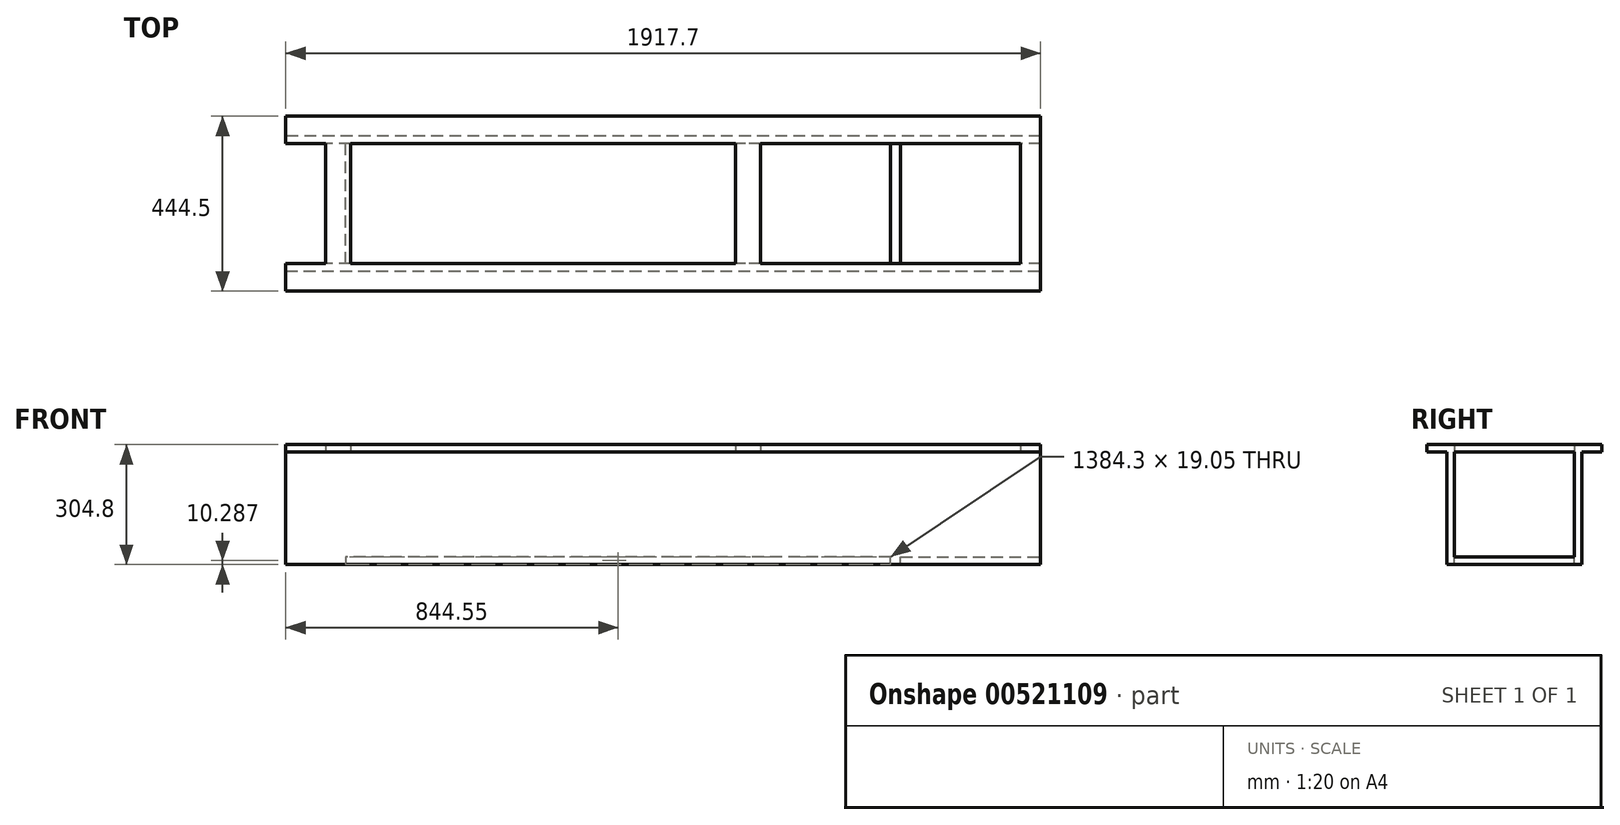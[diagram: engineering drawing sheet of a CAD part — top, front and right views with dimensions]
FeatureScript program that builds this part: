
annotation { "Feature Type Name" : "Feature", "Feature Type Description" : "" }
export const myFeature = defineFeature(function(context is Context, id is Id, definition is map)
    precondition{}
    {
        {
            var Q0;
            Q0=qCreatedBy(makeId("Front.planeOp"),FACE);
            var sketch = newSketch(context, id + "F0", { "sketchPlane" : qUnion([Q0])});
            skLineSegment(sketch, "E0.bottom", {"start": v(831.85, 152.4) * mm, "end": v(-831.85, 152.4) * mm});
            skLineSegment(sketch, "E0.top", {"start": v(831.85, -152.4) * mm, "end": v(-831.85, -152.4) * mm});
            skLineSegment(sketch, "E0.left", {"start": v(831.85, 152.4) * mm, "end": v(831.85, -152.4) * mm});
            skLineSegment(sketch, "E0.right", {"start": v(-831.85, 152.4) * mm, "end": v(-831.85, -152.4) * mm});
            skPoint(sketch, "E0.middle", {"position": v(0, 0) * mm});
            skSolve(sketch);
        }
        {
            var Q0;
            Q0=makeQuery(id+"F0.imprint","IMPRINT",FACE,{"disambiguationData":[TD([[makeQuery(id+"F0.imprint","IMPRINT",EDGE,{"derivedFrom":sQuery(id+"F0.wireOp",EDGE,"E0.bottom")}),1.0]])]});
            extrude(context, id + "F1", {"entities" : qUnion([Q0]), "depth" : 19.05 * mm, "offsetDistance" : 25.4 * mm});
        }
        {
            var Q0;
            Q0=makeQuery(id+"F1.opExtrude","CAP_FACE",FACE,{"disambiguationData":[OSD([sQuery(id+"F0.wireOp",EDGE,"E0.bottom"),sQuery(id+"F0.wireOp",EDGE,"E0.top"),sQuery(id+"F0.wireOp",EDGE,"E0.left"),sQuery(id+"F0.wireOp",EDGE,"E0.right")])],"isStart":false});
            var sketch = newSketch(context, id + "F2", { "sketchPlane" : qUnion([Q0])});
            skLineSegment(sketch, "E1", {"start": v(831.85, -152.4) * mm, "end": v(831.85, -151.64) * mm});
            skLineSegment(sketch, "E2", {"start": v(831.85, -151.64) * mm, "end": v(781.05, -151.64) * mm});
            skLineSegment(sketch, "E3", {"start": v(781.05, -151.64) * mm, "end": v(781.05, -132.59) * mm});
            skLineSegment(sketch, "E4", {"start": v(781.05, -132.59) * mm, "end": v(831.85, -132.59) * mm});
            skLineSegment(sketch, "E5", {"start": v(831.85, -132.59) * mm, "end": v(831.85, -151.64) * mm});
            skSolve(sketch);
        }
        {
            var Q0;
            Q0 = qSketchRegion(id + "F2", true);
            extrude(context, id + "F3", {"entities" : qUnion([Q0]), "operationType" : NewBodyOperationType.ADD, "depth" : 304.8 * mm, "offsetDistance" : 25.4 * mm});
        }
        {
            var Q0;
            Q0=makeQuery(id+"F1.opExtrude","CAP_FACE",FACE,{"disambiguationData":[OSD([sQuery(id+"F0.wireOp",EDGE,"E0.bottom"),sQuery(id+"F0.wireOp",EDGE,"E0.top"),sQuery(id+"F0.wireOp",EDGE,"E0.left"),sQuery(id+"F0.wireOp",EDGE,"E0.right")])],"isStart":false});
            var sketch = newSketch(context, id + "F4", { "sketchPlane" : qUnion([Q0])});
            skLineSegment(sketch, "E6", {"start": v(781.05, -151.64) * mm, "end": v(476.25, -151.64) * mm});
            skLineSegment(sketch, "E7", {"start": v(476.25, -151.64) * mm, "end": v(476.25, -132.59) * mm});
            skLineSegment(sketch, "E8", {"start": v(476.25, -132.59) * mm, "end": v(-831.85, -132.59) * mm});
            skLineSegment(sketch, "E9", {"start": v(476.25, -151.64) * mm, "end": v(-831.85, -151.64) * mm});
            skLineSegment(sketch, "E10", {"start": v(-831.85, -151.64) * mm, "end": v(-831.85, -132.59) * mm});
            skSolve(sketch);
        }
        {
            var Q0;
            Q0=makeQuery(id+"F4.imprint","IMPRINT",FACE,{"disambiguationData":[TD([[makeQuery(id+"F4.imprint","IMPRINT",EDGE,{"derivedFrom":sQuery(id+"F4.wireOp",EDGE,"E7")}),1.0]])]});
            extrude(context, id + "F5", {"entities" : qUnion([Q0]), "operationType" : NewBodyOperationType.ADD, "depth" : 304.8 * mm, "offsetDistance" : 25.4 * mm});
        }
        {
            var Q0;
            Q0=makeQuery(id+"F5.opExtrude","CAP_FACE",FACE,{"disambiguationData":[OSD([sQuery(id+"F4.wireOp",EDGE,"E7"),sQuery(id+"F4.wireOp",EDGE,"E8"),sQuery(id+"F4.wireOp",EDGE,"E9"),sQuery(id+"F4.wireOp",EDGE,"E10")])],"isStart":false});
            var sketch = newSketch(context, id + "F6", { "sketchPlane" : qUnion([Q0])});
            skLineSegment(sketch, "E11", {"start": v(-831.85, -151.64) * mm, "end": v(-831.85, -152.4) * mm});
            skLineSegment(sketch, "E12", {"start": v(-831.85, -152.4) * mm, "end": v(831.85, -152.4) * mm});
            skLineSegment(sketch, "E13", {"start": v(831.85, -152.4) * mm, "end": v(831.85, 152.4) * mm});
            skLineSegment(sketch, "E14", {"start": v(831.85, 152.4) * mm, "end": v(-831.85, 152.4) * mm});
            skLineSegment(sketch, "E15", {"start": v(-831.85, 152.4) * mm, "end": v(-831.85, -152.4) * mm});
            skSolve(sketch);
        }
        {
            var Q0;
            Q0 = qSketchRegion(id + "F6", true);
            extrude(context, id + "F7", {"entities" : qUnion([Q0]), "operationType" : NewBodyOperationType.ADD, "depth" : 19.05 * mm, "offsetDistance" : 25.4 * mm});
        }
        {
            var Q0;
            Q0=makeQuery(id+"F7.opExtrude","SWEPT_FACE",FACE,{"disambiguationData":[OSD([sQuery(id+"F6.wireOp",EDGE,"E14")])]});
            extrude(context, id + "F8", {"entities" : qUnion([Q0]), "operationType" : NewBodyOperationType.REMOVE, "oppositeDirection" : true, "depth" : 19.05 * mm, "offsetDistance" : 25.4 * mm});
        }
        {
            var Q0;
            Q0=makeQuery(id+"F1.opExtrude","SWEPT_FACE",FACE,{"disambiguationData":[OSD([sQuery(id+"F0.wireOp",EDGE,"E0.bottom")])]});
            extrude(context, id + "F9", {"entities" : qUnion([Q0]), "operationType" : NewBodyOperationType.REMOVE, "oppositeDirection" : true, "depth" : 19.05 * mm, "offsetDistance" : 25.4 * mm});
        }
        {
            var Q0;
            Q0=makeQuery(id+"F8.boolean.opBoolean","COPY",FACE,{"derivedFrom":makeQuery(id+"F8.opExtrude","CAP_FACE",FACE,{"disambiguationData":[OSD([sQuery(id+"F6.wireOp",EDGE,"E14")])],"isStart":false})});
            var sketch = newSketch(context, id + "F10", { "sketchPlane" : qUnion([Q0])});
            skLineSegment(sketch, "E16", {"start": v(831.85, -342.9) * mm, "end": v(831.85, -393.7) * mm});
            skLineSegment(sketch, "E17", {"start": v(831.85, -393.7) * mm, "end": v(-831.85, -393.7) * mm});
            skLineSegment(sketch, "E18", {"start": v(-831.85, -393.7) * mm, "end": v(-831.85, -323.85) * mm});
            skLineSegment(sketch, "E19", {"start": v(-831.85, -323.85) * mm, "end": v(-679.45, -323.85) * mm});
            skLineSegment(sketch, "E20", {"start": v(-679.45, -323.85) * mm, "end": v(-679.45, -19.05) * mm});
            skLineSegment(sketch, "E21", {"start": v(-679.45, -19.05) * mm, "end": v(-831.85, -19.05) * mm});
            skLineSegment(sketch, "E22", {"start": v(-831.85, -19.05) * mm, "end": v(-831.85, 50.8) * mm});
            skLineSegment(sketch, "E23", {"start": v(-831.85, 50.8) * mm, "end": v(831.85, 50.8) * mm});
            skLineSegment(sketch, "E24", {"start": v(831.85, 50.8) * mm, "end": v(831.85, -19.05) * mm});
            skLineSegment(sketch, "E25", {"start": v(831.85, -19.05) * mm, "end": v(831.85, -323.85) * mm});
            skLineSegment(sketch, "E26", {"start": v(831.85, -323.85) * mm, "end": v(831.85, -342.9) * mm});
            skLineSegment(sketch, "E27", {"start": v(831.85, -19.05) * mm, "end": v(781.05, -19.05) * mm});
            skLineSegment(sketch, "E28", {"start": v(781.05, -19.05) * mm, "end": v(781.05, -323.85) * mm});
            skLineSegment(sketch, "E29", {"start": v(781.05, -323.85) * mm, "end": v(425.45, -323.85) * mm});
            skLineSegment(sketch, "E30", {"start": v(425.45, -323.85) * mm, "end": v(425.45, -19.05) * mm});
            skLineSegment(sketch, "E31", {"start": v(425.45, -19.05) * mm, "end": v(781.05, -19.05) * mm});
            skLineSegment(sketch, "E32", {"start": v(425.45, -19.05) * mm, "end": v(361.95, -19.05) * mm});
            skLineSegment(sketch, "E33", {"start": v(361.95, -19.05) * mm, "end": v(361.95, -323.85) * mm});
            skLineSegment(sketch, "E34", {"start": v(361.95, -323.85) * mm, "end": v(-679.45, -323.85) * mm});
            skLineSegment(sketch, "E35", {"start": v(-679.45, -323.85) * mm, "end": v(-615.95, -323.85) * mm});
            skLineSegment(sketch, "E36", {"start": v(-615.95, -323.85) * mm, "end": v(-615.95, -19.05) * mm});
            skLineSegment(sketch, "E37", {"start": v(-615.95, -19.05) * mm, "end": v(361.95, -19.05) * mm});
            skSolve(sketch);
        }
        {
            var Q0;
            Q0 = qSketchRegion(id + "F10", true);
            extrude(context, id + "F11", {"entities" : qUnion([Q0]), "operationType" : NewBodyOperationType.ADD, "depth" : 19.05 * mm, "offsetDistance" : 25.4 * mm});
        }
        {
            var Q0;
            Q0=makeQuery(id+"F11.boolean.opBoolean","MERGE",FACE,{"derivedFrom":[makeQuery(id+"F7.opExtrude","CAP_FACE",FACE,{"disambiguationData":[OSD([sQuery(id+"F6.wireOp",EDGE,"E12"),sQuery(id+"F6.wireOp",EDGE,"E13"),sQuery(id+"F6.wireOp",EDGE,"E14"),sQuery(id+"F6.wireOp",EDGE,"E15")])],"isStart":true}),makeQuery(id+"F11.opExtrude","SWEPT_FACE",FACE,{"disambiguationData":[OSD([sQuery(id+"F10.wireOp",EDGE,"E19")])]}),makeQuery(id+"F11.opExtrude","SWEPT_FACE",FACE,{"disambiguationData":[OSD([sQuery(id+"F10.wireOp",EDGE,"E29")])]}),makeQuery(id+"F11.opExtrude","SWEPT_FACE",FACE,{"disambiguationData":[OSD([sQuery(id+"F10.wireOp",EDGE,"E34")])]})]});
            var sketch = newSketch(context, id + "F12", { "sketchPlane" : qUnion([Q0])});
            skLineSegment(sketch, "E38", {"start": v(-476.25, -151.64) * mm, "end": v(-755.65, -151.64) * mm});
            skLineSegment(sketch, "E39", {"start": v(-755.65, -151.64) * mm, "end": v(-755.65, -132.59) * mm});
            skLineSegment(sketch, "E40", {"start": v(-755.65, -132.59) * mm, "end": v(-476.25, -132.59) * mm});
            skLineSegment(sketch, "E41", {"start": v(-476.25, -132.59) * mm, "end": v(-476.25, -151.64) * mm});
            skLineSegment(sketch, "E42", {"start": v(-476.25, -151.64) * mm, "end": v(-479.42, -151.64) * mm});
            skLineSegment(sketch, "E43", {"start": v(-479.42, -151.64) * mm, "end": v(-479.42, -132.59) * mm});
            skSolve(sketch);
        }
        {
            var Q0;
            Q0=makeQuery(id+"F12.imprint","IMPRINT",FACE,{"disambiguationData":[TD([[makeQuery(id+"F12.imprint","IMPRINT",EDGE,{"derivedFrom":sQuery(id+"F12.wireOp",EDGE,"E38")}),-1.0]])]});
            extrude(context, id + "F13", {"entities" : qUnion([Q0]), "operationType" : NewBodyOperationType.ADD, "depth" : 304.8 * mm, "offsetDistance" : 25.4 * mm});
        }
        {
            var Q0;
            Q0=makeQuery(id+"F11.boolean.opBoolean","MERGE",FACE,{"derivedFrom":[makeQuery(id+"F7.boolean.opBoolean","MERGE",FACE,{"derivedFrom":[makeQuery(id+"F5.boolean.opBoolean","MERGE",FACE,{"derivedFrom":[makeQuery(id+"F1.opExtrude","SWEPT_FACE",FACE,{"disambiguationData":[OSD([sQuery(id+"F0.wireOp",EDGE,"E0.right")])]}),makeQuery(id+"F5.opExtrude","SWEPT_FACE",FACE,{"disambiguationData":[OSD([sQuery(id+"F4.wireOp",EDGE,"E10")])]})]}),makeQuery(id+"F7.opExtrude","SWEPT_FACE",FACE,{"disambiguationData":[OSD([sQuery(id+"F6.wireOp",EDGE,"E15")])]})]}),makeQuery(id+"F11.opExtrude","SWEPT_FACE",FACE,{"disambiguationData":[OSD([sQuery(id+"F10.wireOp",EDGE,"E18")])]}),makeQuery(id+"F11.opExtrude","SWEPT_FACE",FACE,{"disambiguationData":[OSD([sQuery(id+"F10.wireOp",EDGE,"E22")])]})]});
            extrude(context, id + "F14", {"entities" : qUnion([Q0]), "operationType" : NewBodyOperationType.REMOVE, "oppositeDirection" : true, "depth" : 50.8 * mm, "offsetDistance" : 25.4 * mm});
        }
        {
            var Q0;
            Q0=makeQuery(id+"F11.boolean.opBoolean","MERGE",FACE,{"derivedFrom":[makeQuery(id+"F7.boolean.opBoolean","MERGE",FACE,{"derivedFrom":[makeQuery(id+"F3.boolean.opBoolean","MERGE",FACE,{"derivedFrom":[makeQuery(id+"F1.opExtrude","SWEPT_FACE",FACE,{"disambiguationData":[OSD([sQuery(id+"F0.wireOp",EDGE,"E0.left")])]}),makeQuery(id+"F3.opExtrude","SWEPT_FACE",FACE,{"disambiguationData":[OSD([sQuery(id+"F2.wireOp",EDGE,"E5")])]})]}),makeQuery(id+"F7.opExtrude","SWEPT_FACE",FACE,{"disambiguationData":[OSD([sQuery(id+"F6.wireOp",EDGE,"E13")])]})]}),makeQuery(id+"F11.opExtrude","SWEPT_FACE",FACE,{"disambiguationData":[OSD([sQuery(id+"F10.wireOp",EDGE,"E16"),sQuery(id+"F10.wireOp",EDGE,"E24"),sQuery(id+"F10.wireOp",EDGE,"E25"),sQuery(id+"F10.wireOp",EDGE,"E26")])]})]});
            extrude(context, id + "F15", {"entities" : qUnion([Q0]), "operationType" : NewBodyOperationType.ADD, "depth" : 304.8 * mm, "offsetDistance" : 25.4 * mm});
        }
        {
            var Q0;
            Q0=makeQuery(id+"F11.opExtrude","SWEPT_FACE",FACE,{"disambiguationData":[OSD([sQuery(id+"F10.wireOp",EDGE,"E28")])]});
            extrude(context, id + "F16", {"entities" : qUnion([Q0]), "operationType" : NewBodyOperationType.REMOVE, "oppositeDirection" : true, "depth" : 304.8 * mm, "offsetDistance" : 25.4 * mm});
        }
        {
            var Q0;
            Q0=makeQuery(id+"F14.boolean.opBoolean","COPY",FACE,{"derivedFrom":makeQuery(id+"F14.opExtrude","CAP_FACE",FACE,{"disambiguationData":[OSD([sQuery(id+"F0.wireOp",EDGE,"E0.right"),sQuery(id+"F4.wireOp",EDGE,"E10"),sQuery(id+"F6.wireOp",EDGE,"E15"),sQuery(id+"F10.wireOp",EDGE,"E18"),sQuery(id+"F10.wireOp",EDGE,"E22")])],"isStart":false})});
            var sketch = newSketch(context, id + "F17", { "sketchPlane" : qUnion([Q0])});
            skLineSegment(sketch, "E44", {"start": v(323.85, -132.59) * mm, "end": v(323.85, -151.64) * mm});
            skLineSegment(sketch, "E45", {"start": v(19.05, -132.59) * mm, "end": v(19.05, -151.64) * mm});
            skSolve(sketch);
        }
        {
            var Q0;
            Q0=makeQuery(id+"F17.imprint","IMPRINT",FACE,{"disambiguationData":[TD([[makeQuery(id+"F17.imprint","IMPRINT",EDGE,{"derivedFrom":sQuery(id+"F17.wireOp",EDGE,"E44")}),-1.0]])]});
            extrude(context, id + "F18", {"entities" : qUnion([Q0]), "operationType" : NewBodyOperationType.REMOVE, "oppositeDirection" : true, "depth" : 152.4 * mm, "offsetDistance" : 25.4 * mm});
        }
    });
